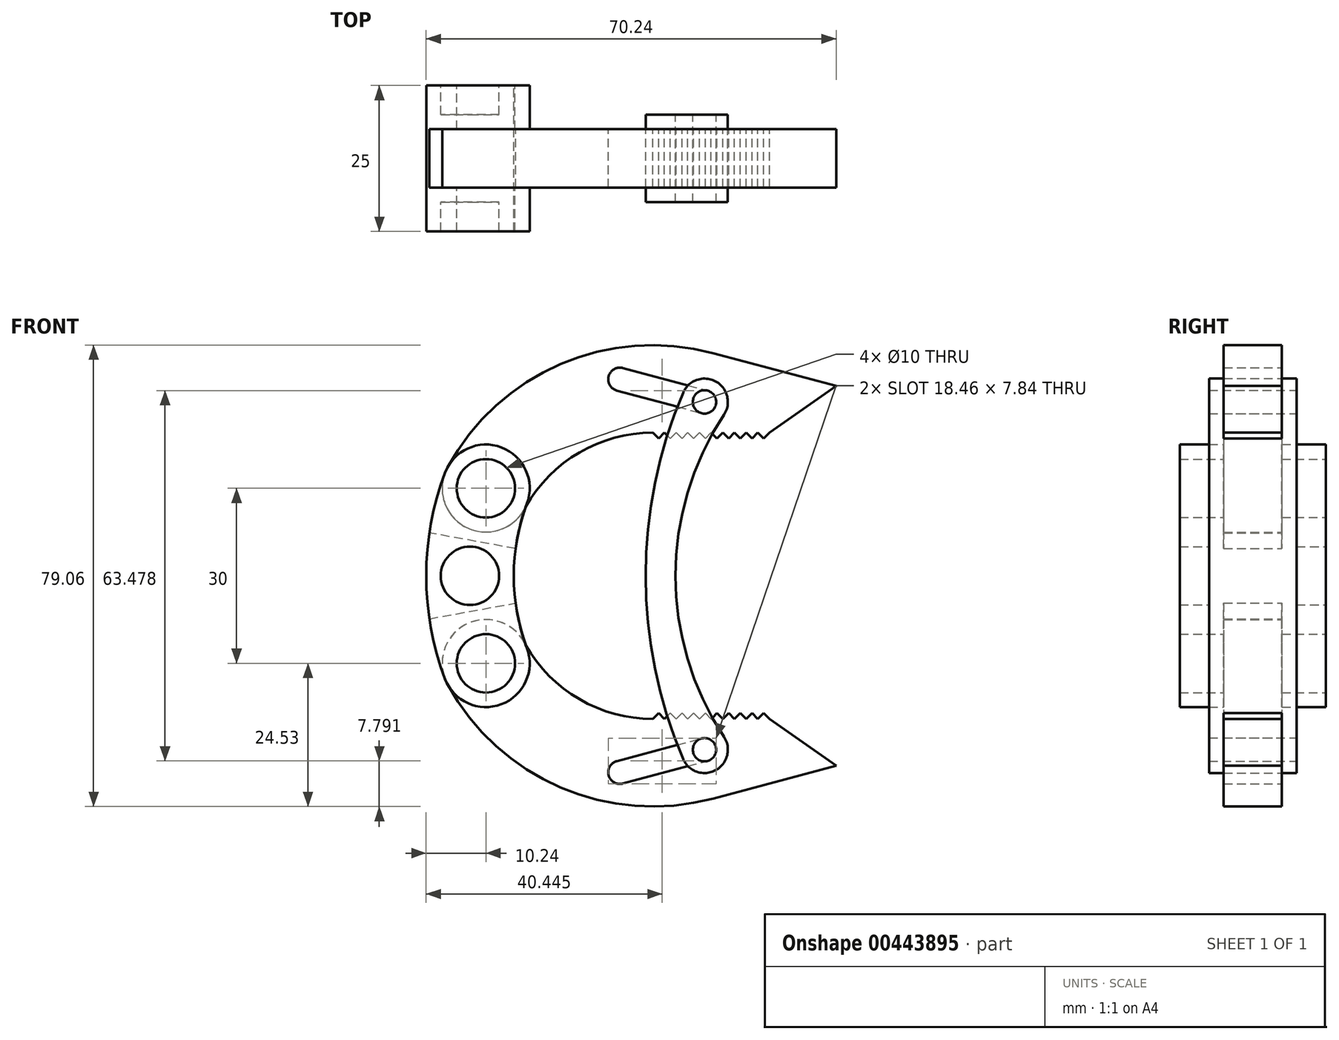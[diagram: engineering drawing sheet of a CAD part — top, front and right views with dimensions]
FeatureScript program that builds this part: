
annotation { "Feature Type Name" : "Feature", "Feature Type Description" : "" }
export const myFeature = defineFeature(function(context is Context, id is Id, definition is map)
    precondition{}
    {
        {
            var Q0;
            Q0=qCreatedBy(makeId("Front.planeOp"),FACE);
            var sketch = newSketch(context, id + "F0", { "sketchPlane" : qUnion([Q0])});
            skLineSegment(sketch, "E0", {"start": v(0, 15) * mm, "end": v(0, -15) * mm, "construction": true});
            skLineSegment(sketch, "E1", {"start": v(0, 0) * mm, "end": v(80, 0) * mm, "construction": true});
            skCircle(sketch, "E2", {"center": v(0, 15) * mm, "radius": 5 * mm});
            skCircle(sketch, "E3", {"center": v(0, -15) * mm, "radius": 5 * mm});
            skArc(sketch, "E4.0", {"start": v(7.02, 12.35) * mm, "mid": v(2.65, 22.02) * mm, "end": v(-7.02, 17.65) * mm});
            skArc(sketch, "E5.0", {"start": v(-7.02, -17.65) * mm, "mid": v(2.65, -22.02) * mm, "end": v(7.02, -12.35) * mm});
            skArc(sketch, "E6", {"start": v(-7.02, 17.65) * mm, "mid": v(-10.24, 0) * mm, "end": v(-7.02, -17.65) * mm});
            skArc(sketch, "E7", {"start": v(7.02, 12.35) * mm, "mid": v(4.76, 0) * mm, "end": v(7.02, -12.35) * mm});
            skCircle(sketch, "E8", {"center": v(-2.74, 0) * mm, "radius": 5 * mm});
            skArc(sketch, "E9", {"start": v(0, 15) * mm, "mid": v(-2.74, 0) * mm, "end": v(0, -15) * mm, "construction": true});
            skCircle(sketch, "E10.0", {"center": v(-2.74, 0) * mm, "radius": 6 * mm, "construction": true});
            skCircle(sketch, "E11.0", {"center": v(0, -15) * mm, "radius": 9.25 * mm, "construction": true});
            skLineSegment(sketch, "E12", {"start": v(-9.69, -7.37) * mm, "end": v(5.08, -4.67) * mm});
            skLineSegment(sketch, "E13", {"start": v(5.08, 4.67) * mm, "end": v(-9.69, 7.37) * mm});
            skSolve(sketch);
        }
        {
            var Q0;
            Q0 = qSketchRegion(id + "F0", true);
            extrude(context, id + "F1", {"entities" : qUnion([Q0]), "endBound" : BoundingType.SYMMETRIC, "depth" : 25 * mm});
        }
        {
            var Q0;
            Q0=makeQuery(id+"F0.imprint","IMPRINT",FACE,{"disambiguationData":[TD([[makeQuery(id+"F0.imprint","IMPRINT",EDGE,{"derivedFrom":sQuery(id+"F0.wireOp",EDGE,"E2")}),-1.0]])]});
            var Q1;
            Q1=makeQuery(id+"F0.imprint","IMPRINT",FACE,{"disambiguationData":[TD([[makeQuery(id+"F0.imprint","IMPRINT",EDGE,{"derivedFrom":sQuery(id+"F0.wireOp",EDGE,"E3")}),-1.0]])]});
            extrude(context, id + "F2", {"entities" : qUnion([Q0, Q1]), "operationType" : NewBodyOperationType.REMOVE, "endBound" : BoundingType.SYMMETRIC, "depth" : 10 * mm});
        }
        {
            var Q0;
            Q0=qCreatedBy(makeId("Front.planeOp"),FACE);
            var sketch = newSketch(context, id + "F3", { "sketchPlane" : qUnion([Q0])});
            skCircle(sketch, "E14.0", {"center": v(0, 15) * mm, "radius": 7.5 * mm});
            skArc(sketch, "E15", {"start": v(-6.6, 18.57) * mm, "mid": v(12.76, 36.27) * mm, "end": v(38.92, 38.17) * mm});
            skArc(sketch, "E16", {"start": v(6.6, 11.43) * mm, "mid": v(15.79, 21) * mm, "end": v(28.58, 24.53) * mm});
            skLineSegment(sketch, "E17", {"start": v(28.58, 24.53) * mm, "end": v(48.58, 24.53) * mm});
            skLineSegment(sketch, "E18", {"start": v(48.58, 24.53) * mm, "end": v(60, 32.53) * mm});
            skLineSegment(sketch, "E19", {"start": v(60, 32.53) * mm, "end": v(38.92, 38.17) * mm});
            skLineSegment(sketch, "E20", {"start": v(37.45, 29.8) * mm, "end": v(22.96, 33.68) * mm});
            skArc(sketch, "E21", {"start": v(23.48, 35.6) * mm, "mid": v(21.03, 34.2) * mm, "end": v(22.44, 31.75) * mm});
            skArc(sketch, "E22", {"start": v(36.93, 27.87) * mm, "mid": v(39.38, 29.28) * mm, "end": v(37.97, 31.73) * mm});
            skLineSegment(sketch, "E23", {"start": v(23.48, 35.6) * mm, "end": v(37.97, 31.73) * mm});
            skLineSegment(sketch, "E24", {"start": v(22.44, 31.75) * mm, "end": v(36.93, 27.87) * mm});
            skLineSegment(sketch, "E25", {"start": v(38.92, 38.17) * mm, "end": v(37.45, 29.8) * mm});
            skLineSegment(sketch, "E26", {"start": v(28.58, 24.53) * mm, "end": v(29.58, 23.53) * mm});
            skLineSegment(sketch, "E27", {"start": v(29.58, 23.53) * mm, "end": v(30.58, 24.53) * mm});
            skLineSegment(sketch, "E28.1.0.0", {"start": v(31.58, 23.53) * mm, "end": v(32.58, 24.53) * mm});
            skLineSegment(sketch, "E28.1.0.1", {"start": v(30.58, 24.53) * mm, "end": v(31.58, 23.53) * mm});
            skLineSegment(sketch, "E28.2.0.0", {"start": v(33.58, 23.53) * mm, "end": v(34.58, 24.53) * mm});
            skLineSegment(sketch, "E28.2.0.1", {"start": v(32.58, 24.53) * mm, "end": v(33.58, 23.53) * mm});
            skLineSegment(sketch, "E28.3.0.0", {"start": v(35.58, 23.53) * mm, "end": v(36.58, 24.53) * mm});
            skLineSegment(sketch, "E28.3.0.1", {"start": v(34.58, 24.53) * mm, "end": v(35.58, 23.53) * mm});
            skLineSegment(sketch, "E28.4.0.0", {"start": v(37.58, 23.53) * mm, "end": v(38.58, 24.53) * mm});
            skLineSegment(sketch, "E28.4.0.1", {"start": v(36.58, 24.53) * mm, "end": v(37.58, 23.53) * mm});
            skLineSegment(sketch, "E28.5.0.0", {"start": v(39.58, 23.53) * mm, "end": v(40.58, 24.53) * mm});
            skLineSegment(sketch, "E28.5.0.1", {"start": v(38.58, 24.53) * mm, "end": v(39.58, 23.53) * mm});
            skLineSegment(sketch, "E28.6.0.0", {"start": v(41.58, 23.53) * mm, "end": v(42.58, 24.53) * mm});
            skLineSegment(sketch, "E28.6.0.1", {"start": v(40.58, 24.53) * mm, "end": v(41.58, 23.53) * mm});
            skLineSegment(sketch, "E28.7.0.0", {"start": v(43.58, 23.53) * mm, "end": v(44.58, 24.53) * mm});
            skLineSegment(sketch, "E28.7.0.1", {"start": v(42.58, 24.53) * mm, "end": v(43.58, 23.53) * mm});
            skLineSegment(sketch, "E28.8.0.0", {"start": v(45.58, 23.53) * mm, "end": v(46.58, 24.53) * mm});
            skLineSegment(sketch, "E28.8.0.1", {"start": v(44.58, 24.53) * mm, "end": v(45.58, 23.53) * mm});
            skLineSegment(sketch, "E28.9.0.0", {"start": v(47.58, 23.53) * mm, "end": v(48.58, 24.53) * mm});
            skLineSegment(sketch, "E28.9.0.1", {"start": v(46.58, 24.53) * mm, "end": v(47.58, 23.53) * mm});
            skLineSegment(sketch, "E28.direction1", {"start": v(29.58, 23.53) * mm, "end": v(31.58, 23.53) * mm, "construction": true});
            skLineSegment(sketch, "E29.MirrorCS", {"start": v(29.58, -23.53) * mm, "end": v(30.58, -24.53) * mm});
            skLineSegment(sketch, "E30.MirrorCS", {"start": v(35.58, -23.53) * mm, "end": v(36.58, -24.53) * mm});
            skLineSegment(sketch, "E31.MirrorCS", {"start": v(44.58, -24.53) * mm, "end": v(45.58, -23.53) * mm});
            skLineSegment(sketch, "E32.MirrorCS", {"start": v(32.58, -24.53) * mm, "end": v(33.58, -23.53) * mm});
            skLineSegment(sketch, "E33.MirrorCS", {"start": v(38.58, -24.53) * mm, "end": v(39.58, -23.53) * mm});
            skLineSegment(sketch, "E34.MirrorCS", {"start": v(29.58, -23.53) * mm, "end": v(31.58, -23.53) * mm, "construction": true});
            skLineSegment(sketch, "E35.MirrorCS", {"start": v(41.58, -23.53) * mm, "end": v(42.58, -24.53) * mm});
            skLineSegment(sketch, "E36.MirrorCS", {"start": v(30.58, -24.53) * mm, "end": v(31.58, -23.53) * mm});
            skLineSegment(sketch, "E37.MirrorCS", {"start": v(47.58, -23.53) * mm, "end": v(48.58, -24.53) * mm});
            skLineSegment(sketch, "E38.MirrorCS", {"start": v(45.58, -23.53) * mm, "end": v(46.58, -24.53) * mm});
            skLineSegment(sketch, "E39.MirrorCS", {"start": v(46.58, -24.53) * mm, "end": v(47.58, -23.53) * mm});
            skLineSegment(sketch, "E40.MirrorCS", {"start": v(39.58, -23.53) * mm, "end": v(40.58, -24.53) * mm});
            skLineSegment(sketch, "E41.MirrorCS", {"start": v(28.58, -24.53) * mm, "end": v(29.58, -23.53) * mm});
            skLineSegment(sketch, "E42.MirrorCS", {"start": v(40.58, -24.53) * mm, "end": v(41.58, -23.53) * mm});
            skLineSegment(sketch, "E43.MirrorCS", {"start": v(31.58, -23.53) * mm, "end": v(32.58, -24.53) * mm});
            skLineSegment(sketch, "E44.MirrorCS", {"start": v(42.58, -24.53) * mm, "end": v(43.58, -23.53) * mm});
            skLineSegment(sketch, "E45.MirrorCS", {"start": v(43.58, -23.53) * mm, "end": v(44.58, -24.53) * mm});
            skLineSegment(sketch, "E46.MirrorCS", {"start": v(34.58, -24.53) * mm, "end": v(35.58, -23.53) * mm});
            skLineSegment(sketch, "E47.MirrorCS", {"start": v(33.58, -23.53) * mm, "end": v(34.58, -24.53) * mm});
            skLineSegment(sketch, "E48.MirrorCS", {"start": v(36.58, -24.53) * mm, "end": v(37.58, -23.53) * mm});
            skLineSegment(sketch, "E49.MirrorCS", {"start": v(28.58, -24.53) * mm, "end": v(48.58, -24.53) * mm});
            skLineSegment(sketch, "E50.MirrorCS", {"start": v(37.58, -23.53) * mm, "end": v(38.58, -24.53) * mm});
            skLineSegment(sketch, "E51.MirrorCS", {"start": v(38.92, -38.17) * mm, "end": v(37.45, -29.8) * mm});
            skLineSegment(sketch, "E52.MirrorCS", {"start": v(22.44, -31.75) * mm, "end": v(36.93, -27.87) * mm});
            skArc(sketch, "E53.MirrorCS", {"start": v(23.48, -35.6) * mm, "mid": v(21.03, -34.2) * mm, "end": v(22.44, -31.75) * mm});
            skCircle(sketch, "E54.MirrorC", {"center": v(0, -15) * mm, "radius": 7.5 * mm});
            skLineSegment(sketch, "E55.MirrorCS", {"start": v(37.45, -29.8) * mm, "end": v(22.96, -33.68) * mm});
            skArc(sketch, "E56.MirrorCS", {"start": v(6.6, -11.43) * mm, "mid": v(15.79, -21) * mm, "end": v(28.58, -24.53) * mm});
            skLineSegment(sketch, "E57.MirrorCS", {"start": v(60, -32.53) * mm, "end": v(38.92, -38.17) * mm});
            skArc(sketch, "E58.MirrorCS", {"start": v(36.93, -27.87) * mm, "mid": v(39.38, -29.28) * mm, "end": v(37.97, -31.73) * mm});
            skLineSegment(sketch, "E59.MirrorCS", {"start": v(48.58, -24.53) * mm, "end": v(60, -32.53) * mm});
            skArc(sketch, "E60.MirrorCS", {"start": v(-6.6, -18.57) * mm, "mid": v(12.76, -36.27) * mm, "end": v(38.92, -38.17) * mm});
            skLineSegment(sketch, "E61.MirrorCS", {"start": v(23.48, -35.6) * mm, "end": v(37.97, -31.73) * mm});
            skSolve(sketch);
        }
        {
            var Q0;
            Q0=qCreatedBy(makeId("Front.planeOp"),FACE);
            var sketch = newSketch(context, id + "F4", { "sketchPlane" : qUnion([Q0])});
            skArc(sketch, "E62.0.1", {"start": v(-6.6, 18.57) * mm, "mid": v(3.57, 21.6) * mm, "end": v(6.6, 11.43) * mm});
            skArc(sketch, "E62.0.2", {"start": v(6.6, 11.43) * mm, "mid": v(15.79, 21) * mm, "end": v(28.58, 24.53) * mm});
            skLineSegment(sketch, "E62.0.3", {"start": v(28.58, 24.53) * mm, "end": v(30.58, 24.53) * mm});
            skLineSegment(sketch, "E62.0.4", {"start": v(30.58, 24.53) * mm, "end": v(32.58, 24.53) * mm});
            skLineSegment(sketch, "E62.0.5", {"start": v(31.22, 24.53) * mm, "end": v(32.58, 24.53) * mm});
            skLineSegment(sketch, "E62.0.8", {"start": v(38.91, 24.53) * mm, "end": v(40.58, 24.53) * mm});
            skLineSegment(sketch, "E62.0.9", {"start": v(40.58, 24.53) * mm, "end": v(42.58, 24.53) * mm});
            skLineSegment(sketch, "E62.0.10", {"start": v(42.58, 24.53) * mm, "end": v(44.58, 24.53) * mm});
            skLineSegment(sketch, "E62.0.11", {"start": v(44.58, 24.53) * mm, "end": v(46.58, 24.53) * mm});
            skLineSegment(sketch, "E62.0.12", {"start": v(46.58, 24.53) * mm, "end": v(48.58, 24.53) * mm});
            skLineSegment(sketch, "E62.0.13", {"start": v(48.58, 24.53) * mm, "end": v(60, 32.53) * mm});
            skLineSegment(sketch, "E62.0.14", {"start": v(60, 32.53) * mm, "end": v(38.92, 38.17) * mm});
            skLineSegment(sketch, "E63.0", {"start": v(23.48, 35.6) * mm, "end": v(34.62, 32.63) * mm});
            skArc(sketch, "E63.1", {"start": v(36.93, 27.87) * mm, "mid": v(39.38, 29.28) * mm, "end": v(37.97, 31.73) * mm});
            skLineSegment(sketch, "E63.2", {"start": v(22.44, 31.75) * mm, "end": v(32.8, 28.98) * mm});
            skArc(sketch, "E63.3", {"start": v(23.48, 35.6) * mm, "mid": v(21.03, 34.2) * mm, "end": v(22.44, 31.75) * mm});
            skArc(sketch, "E64", {"start": v(40.79, 27.6) * mm, "mid": v(39.35, 33.32) * mm, "end": v(33.77, 31.37) * mm});
            skArc(sketch, "E65", {"start": v(33.77, 31.37) * mm, "mid": v(27.36, 0) * mm, "end": v(33.77, -31.37) * mm});
            skArc(sketch, "E66", {"start": v(40.79, 27.6) * mm, "mid": v(32.48, 0) * mm, "end": v(40.79, -27.6) * mm});
            skCircle(sketch, "E67", {"center": v(37.45, 29.8) * mm, "radius": 2 * mm});
            skPoint(sketch, "E62.0.6.start.orphan", {"position": v(34.58, 24.53) * mm});
            skPoint(sketch, "E62.0.7.start.orphan", {"position": v(36.58, 24.53) * mm});
            skPoint(sketch, "E68.orphan", {"position": v(38.58, 24.53) * mm});
            skPoint(sketch, "E69.orphan", {"position": v(36.93, 27.87) * mm});
            skPoint(sketch, "E70.orphan", {"position": v(37.97, 31.73) * mm});
            skLineSegment(sketch, "E71.MirrorCS", {"start": v(60, -32.53) * mm, "end": v(38.92, -38.17) * mm});
            skArc(sketch, "E72.MirrorCS", {"start": v(6.6, -11.43) * mm, "mid": v(15.79, -21) * mm, "end": v(28.58, -24.53) * mm});
            skLineSegment(sketch, "E73.MirrorCS", {"start": v(48.58, -24.53) * mm, "end": v(60, -32.53) * mm});
            skArc(sketch, "E74.MirrorCS", {"start": v(-6.6, -18.57) * mm, "mid": v(3.57, -21.6) * mm, "end": v(6.6, -11.43) * mm});
            skLineSegment(sketch, "E75.MirrorCS", {"start": v(31.22, -24.53) * mm, "end": v(32.58, -24.53) * mm});
            skLineSegment(sketch, "E76.MirrorCS", {"start": v(46.58, -24.53) * mm, "end": v(48.58, -24.53) * mm});
            skLineSegment(sketch, "E77.MirrorCS", {"start": v(38.91, -24.53) * mm, "end": v(40.58, -24.53) * mm});
            skLineSegment(sketch, "E78.MirrorCS", {"start": v(30.58, -24.53) * mm, "end": v(32.58, -24.53) * mm});
            skLineSegment(sketch, "E79.MirrorCS", {"start": v(42.58, -24.53) * mm, "end": v(44.58, -24.53) * mm});
            skLineSegment(sketch, "E80.MirrorCS", {"start": v(40.58, -24.53) * mm, "end": v(42.58, -24.53) * mm});
            skLineSegment(sketch, "E81.MirrorCS", {"start": v(28.58, -24.53) * mm, "end": v(30.58, -24.53) * mm});
            skLineSegment(sketch, "E82.MirrorCS", {"start": v(44.58, -24.53) * mm, "end": v(46.58, -24.53) * mm});
            skArc(sketch, "E83.MirrorCS", {"start": v(36.93, -27.87) * mm, "mid": v(39.38, -29.28) * mm, "end": v(37.97, -31.73) * mm});
            skPoint(sketch, "E84.MirrorP", {"position": v(34.58, -24.53) * mm});
            skArc(sketch, "E85.MirrorC", {"start": v(40.79, -27.6) * mm, "mid": v(39.35, -33.32) * mm, "end": v(33.77, -31.37) * mm});
            skPoint(sketch, "E86.MirrorP", {"position": v(36.58, -24.53) * mm});
            skCircle(sketch, "E87.MirrorC", {"center": v(37.45, -29.8) * mm, "radius": 2 * mm});
            skLineSegment(sketch, "E88.MirrorCS", {"start": v(23.48, -35.6) * mm, "end": v(34.62, -32.63) * mm});
            skLineSegment(sketch, "E89.MirrorCS", {"start": v(22.44, -31.75) * mm, "end": v(32.8, -28.98) * mm});
            skPoint(sketch, "E90.MirrorP", {"position": v(36.93, -27.87) * mm});
            skPoint(sketch, "E91.MirrorP", {"position": v(38.58, -24.53) * mm});
            skPoint(sketch, "E92.MirrorP", {"position": v(37.97, -31.73) * mm});
            skArc(sketch, "E93.MirrorCS", {"start": v(23.48, -35.6) * mm, "mid": v(21.03, -34.2) * mm, "end": v(22.44, -31.75) * mm});
            skSolve(sketch);
        }
        {
            var Q0;
            {var subQ7=sQuery(id+"F4.wireOp",EDGE,"E65");var subQ11=makeQuery(id+"F4.imprint","IMPRINT",VERTEX,{"disambiguationData":[OD(0.0)],"derivedFrom":subQ7});Q0=makeQuery(id+"F4.imprint","IMPRINT",FACE,{"disambiguationData":[TD([[makeQuery(id+"F4.imprint","IMPRINT",EDGE,{"disambiguationData":[TD([[subQ11,-1.0]])],"derivedFrom":subQ7}),1.0]])]});}
            extrude(context, id + "F5", {"entities" : qUnion([Q0]), "endBound" : BoundingType.SYMMETRIC, "depth" : 15 * mm});
        }
        {
            var Q0;
            Q0 = qSketchRegion(id + "F3", true);
            extrude(context, id + "F6", {"entities" : qUnion([Q0]), "endBound" : BoundingType.SYMMETRIC, "depth" : 10 * mm});
        }
        {
            var Q0;
            Q0=makeQuery(id+"F0.imprint","IMPRINT",FACE,{"disambiguationData":[TD([[makeQuery(id+"F0.imprint","IMPRINT",EDGE,{"derivedFrom":sQuery(id+"F0.wireOp",EDGE,"E8")}),1.0]])]});
            extrude(context, id + "F8", {"entities" : qUnion([Q0]), "operationType" : NewBodyOperationType.ADD, "endBound" : BoundingType.SYMMETRIC, "depth" : 15 * mm});
        }
        {
            var Q0;
            Q0=makeQuery(id+"F0.imprint","IMPRINT",FACE,{"disambiguationData":[TD([[makeQuery(id+"F0.imprint","IMPRINT",EDGE,{"derivedFrom":sQuery(id+"F0.wireOp",EDGE,"E8")}),1.0]])]});
            extrude(context, id + "F10", {"entities" : qUnion([Q0]), "operationType" : NewBodyOperationType.ADD, "endBound" : BoundingType.SYMMETRIC, "depth" : 15 * mm});
        }
    });
